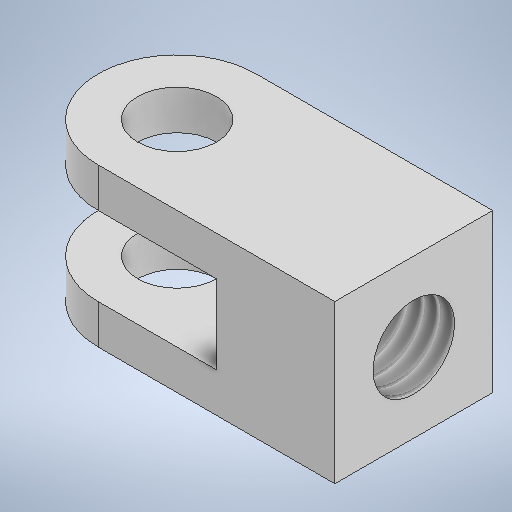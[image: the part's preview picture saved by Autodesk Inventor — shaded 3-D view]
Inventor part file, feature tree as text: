
AUTODESK INVENTOR PART (.ipt)
format: ipt  version: 2025.1 (Build 291241000, 241)  size: 295,936 bytes
history: native  units: mm
features: sketch x4, extrude x2, hole x2
ambient origin geometry x8: Origin, YZ Plane, XZ Plane, XY Plane, X Axis, Y Axis, Z Axis, Center Point
bodies: Solid1 (feature_tree)
feature tree (8):
  extrude  "Extrusion1"  Depth=12.0mm
  hole  "Hole1"  [1 undecoded]
  extrude  "Extrusion2"  Depth=4.0mm
  hole  "Hole2"  [1 undecoded]
  sketch  "Sketch1"  dims[d0=4.0mm d1=12.0mm]
  sketch  "Sketch2"  dims[d2=8.0mm d3=8.0mm d4=0.0mm]
  sketch  "Sketch3"  dims[d5=10.0mm d6=4.0mm]
  sketch  "Sketch4"  dims[d7=8.0mm d8=0.0mm d9=4.0mm d10=6.0mm d11=4.0mm d12=2.0mm d13=90.0deg d14=8.0mm d15=0.0mm d16=4.134mm d17=10.0mm d18=4.0mm d19=2.0mm d20=90.0deg d21=8.0mm d22=0.0mm]
note: 2 required parameter values undecoded (feature->parameter linkage not recoverable at this tier; creation-order binding heuristic only, values carry confidence <= 0.55)
